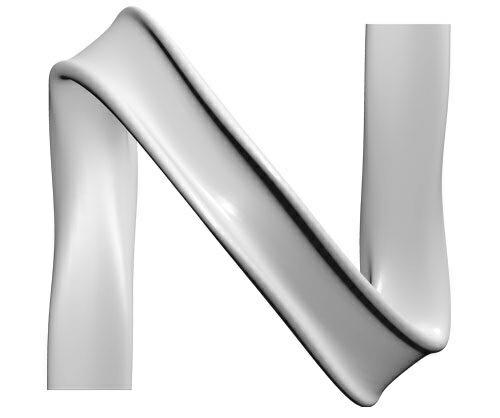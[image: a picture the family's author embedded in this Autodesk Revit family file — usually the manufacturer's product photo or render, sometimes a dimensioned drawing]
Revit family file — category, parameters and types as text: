
# Revit family: CITY ALPHABET letter „N”
name_source: partatom
category: Furniture
revit_build: Autodesk Revit 2018 (Build: 20190510_1515(x64)
units: mm (PartAtom-declared; Revit-internal decimal feet)

## family parameters
Cut with Voids When Loaded = No
Host = Face
OmniClass Number = 23.40.10.11.14
OmniClass Title = Exterior Seating
Room Calculation Point = No
Shared = No

## types (1)
- CITY ALPHABET letter „N”
    Default Elevation = 1219 mm
    Height = 1250 mm  [stored 4.10105 ft]
    IfcExportAs = IfcFurnishingElement
    Length = 2260 mm  [stored 7.4147 ft]
    Manufacturer = Astrini Design
    Material information = Colour choice from RAL colour standard. Customer may inquire about specific request regarding individual order.
    Model = CITY ALPHABET letter „N”
    Operating temperature = -40°C to 80°C, ( -40°F to 176°F )
    Type Comments = Bench
    Type Image = N.jpg
    URL = https://astrini-design.pl
    Weight (approximately) = 75.00 kg
    Weight - filled (approximately) = 125.00 kg
    Width = 2280 mm  [stored 7.48031 ft]

note: [stored X ft] marks values corroborated as IEEE doubles in the binary element streams (Revit-internal decimal feet)
